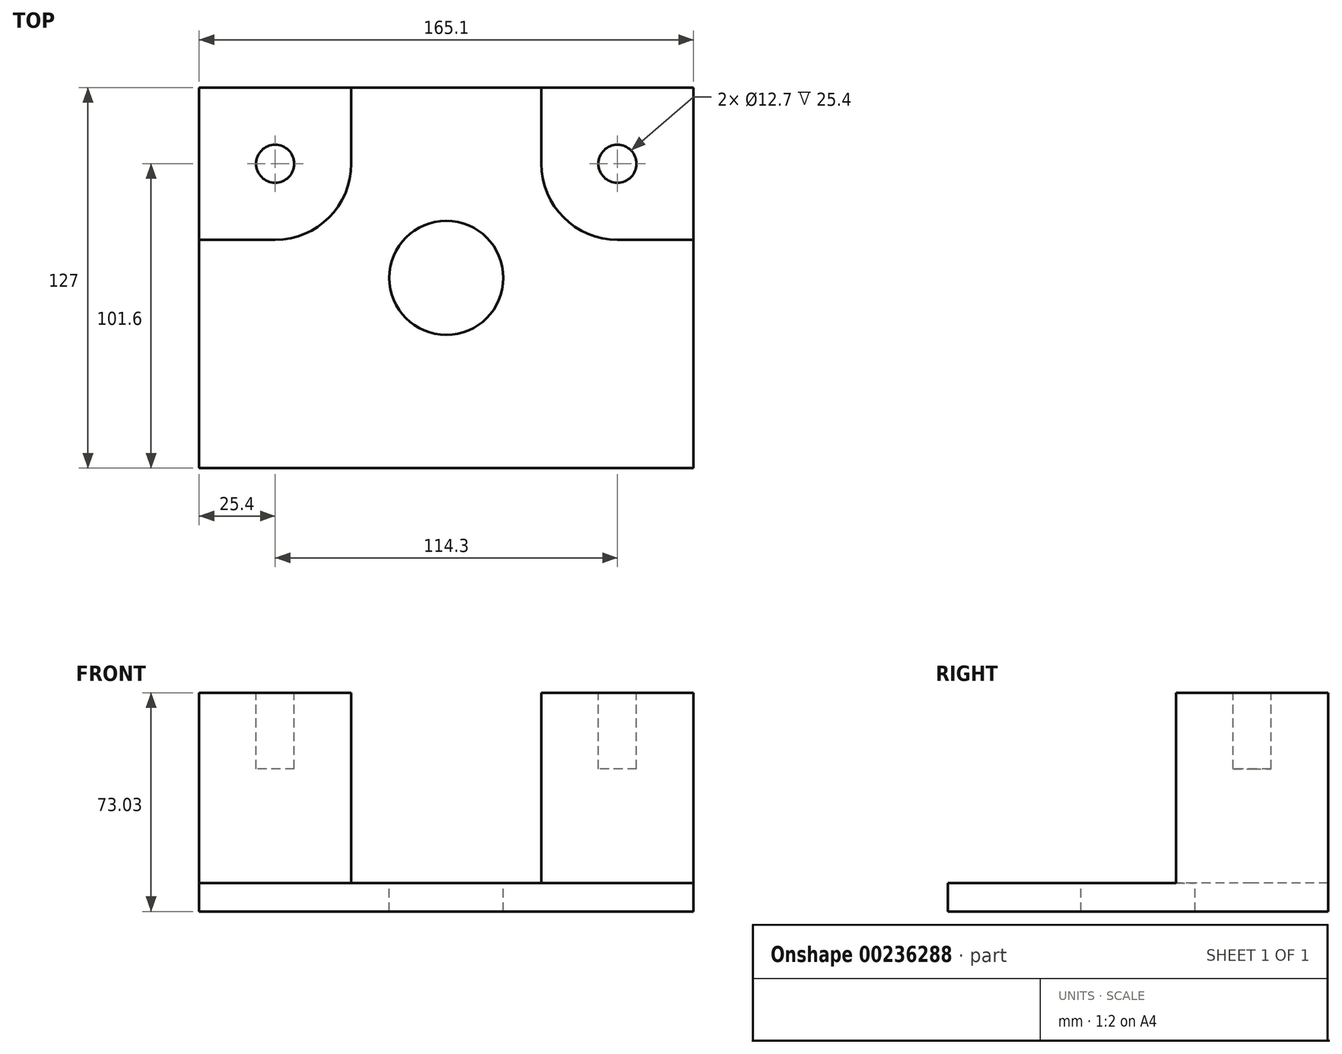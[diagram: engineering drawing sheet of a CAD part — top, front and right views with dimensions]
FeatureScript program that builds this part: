
annotation { "Feature Type Name" : "Feature", "Feature Type Description" : "" }
export const myFeature = defineFeature(function(context is Context, id is Id, definition is map)
    precondition{}
    {
        {
            var Q0;
            Q0=qCreatedBy(makeId("Top.planeOp"),FACE);
            var sketch = newSketch(context, id + "F0", { "sketchPlane" : qUnion([Q0])});
            skLineSegment(sketch, "E0.bottom", {"start": v(82.55, 63.5) * mm, "end": v(-82.55, 63.5) * mm});
            skLineSegment(sketch, "E0.top", {"start": v(82.55, -63.5) * mm, "end": v(-82.55, -63.5) * mm});
            skLineSegment(sketch, "E0.left", {"start": v(82.55, 63.5) * mm, "end": v(82.55, -63.5) * mm});
            skLineSegment(sketch, "E0.right", {"start": v(-82.55, 63.5) * mm, "end": v(-82.55, -63.5) * mm});
            skPoint(sketch, "E0.middle", {"position": v(0, 0) * mm});
            skSolve(sketch);
        }
        {
            var Q0;
            Q0 = qSketchRegion(id + "F0", true);
            extrude(context, id + "F1", {"entities" : qUnion([Q0]), "depth" : 9.52 * mm});
        }
        {
            var Q0;
            Q0=makeQuery(id+"F1.opExtrude","CAP_FACE",FACE,{"disambiguationData":[OSD([sQuery(id+"F0.wireOp",EDGE,"E0.bottom"),sQuery(id+"F0.wireOp",EDGE,"E0.top"),sQuery(id+"F0.wireOp",EDGE,"E0.left"),sQuery(id+"F0.wireOp",EDGE,"E0.right")])],"isStart":false});
            var sketch = newSketch(context, id + "F2", { "sketchPlane" : qUnion([Q0])});
            skLineSegment(sketch, "E1.bottom", {"start": v(-82.55, 63.5) * mm, "end": v(-31.75, 63.5) * mm});
            skLineSegment(sketch, "E1.top", {"start": v(-82.55, 12.7) * mm, "end": v(-57.15, 12.7) * mm});
            skLineSegment(sketch, "E1.left", {"start": v(-82.55, 63.5) * mm, "end": v(-82.55, 12.7) * mm});
            skLineSegment(sketch, "E1.right", {"start": v(-31.75, 63.5) * mm, "end": v(-31.75, 38.1) * mm});
            skLineSegment(sketch, "E2.bottom", {"start": v(82.55, 63.5) * mm, "end": v(31.75, 63.5) * mm});
            skLineSegment(sketch, "E2.top", {"start": v(82.55, 12.7) * mm, "end": v(57.15, 12.7) * mm});
            skLineSegment(sketch, "E2.left", {"start": v(82.55, 63.5) * mm, "end": v(82.55, 12.7) * mm});
            skLineSegment(sketch, "E2.right", {"start": v(31.75, 63.5) * mm, "end": v(31.75, 38.1) * mm});
            skPoint(sketch, "E3.visualSharp", {"position": v(-31.75, 12.7) * mm});
            skArc(sketch, "E3.filletArc", {"start": v(-57.15, 12.7) * mm, "mid": v(-39.19, 20.14) * mm, "end": v(-31.75, 38.1) * mm});
            skPoint(sketch, "E4.visualSharp", {"position": v(31.75, 12.7) * mm});
            skArc(sketch, "E4.filletArc", {"start": v(31.75, 38.1) * mm, "mid": v(39.19, 20.14) * mm, "end": v(57.15, 12.7) * mm});
            skSolve(sketch);
        }
        {
            var Q0;
            Q0=makeQuery(id+"F2.imprint","IMPRINT",FACE,{"disambiguationData":[TD([[makeQuery(id+"F2.imprint","IMPRINT",EDGE,{"derivedFrom":sQuery(id+"F2.wireOp",EDGE,"E1.bottom")}),1.0]])]});
            var Q1;
            Q1=makeQuery(id+"F2.imprint","IMPRINT",FACE,{"disambiguationData":[TD([[makeQuery(id+"F2.imprint","IMPRINT",EDGE,{"derivedFrom":sQuery(id+"F2.wireOp",EDGE,"E2.bottom")}),1.0]])]});
            extrude(context, id + "F3", {"entities" : qUnion([Q0, Q1]), "operationType" : NewBodyOperationType.ADD, "depth" : 63.5 * mm});
        }
        {
            var Q0;
            {var subQ0=sQuery(id+"F0.wireOp",EDGE,"E0.left");var subQ1=sQuery(id+"F0.wireOp",EDGE,"E0.bottom");var subQ2=sQuery(id+"F0.wireOp",EDGE,"E0.top");var subQ3=sQuery(id+"F0.wireOp",EDGE,"E0.right");Q0=makeQuery(id+"F3.boolean.opBoolean","SPLIT",FACE,{"disambiguationData":[TD([makeQuery(id+"F1.opExtrude","SWEPT_FACE",FACE,{"disambiguationData":[OSD([subQ1])]})])],"derivedFrom":makeQuery(id+"F1.opExtrude","CAP_FACE",FACE,{"disambiguationData":[OSD([subQ1,subQ2,subQ0,subQ3])],"isStart":false})});}
            var sketch = newSketch(context, id + "F4", { "sketchPlane" : qUnion([Q0])});
            skCircle(sketch, "E5", {"center": v(0, 0) * mm, "radius": 19.84 * mm});
            skSolve(sketch);
        }
        {
            var Q0;
            Q0=sQuery(id+"F4.wireOp",VERTEX,"E5.center");
            var Q1;
            Q1=makeQuery(id+"F1.opExtrude","SWEPT_BODY",BODY,{"disambiguationData":[OSD([sQuery(id+"F0.wireOp",EDGE,"E0.bottom"),sQuery(id+"F0.wireOp",EDGE,"E0.top"),sQuery(id+"F0.wireOp",EDGE,"E0.left"),sQuery(id+"F0.wireOp",EDGE,"E0.right")])]});
            hole(context, id + "F5", {"style" : HoleStyle.SIMPLE, "endStyle" : HoleEndStyle.THROUGH, "holeDiameter" : 38.1 * mm, "locations" : qUnion([Q0]), "scope" : qUnion([Q1]), "isTappedThrough" : true});
        }
        {
            var Q0;
            Q0=makeQuery(id+"F3.opExtrude","CAP_FACE",FACE,{"disambiguationData":[OSD([sQuery(id+"F2.wireOp",EDGE,"E1.bottom"),sQuery(id+"F2.wireOp",EDGE,"E1.top"),sQuery(id+"F2.wireOp",EDGE,"E1.left"),sQuery(id+"F2.wireOp",EDGE,"E1.right"),sQuery(id+"F2.wireOp",EDGE,"E3.filletArc")])],"isStart":false});
            var sketch = newSketch(context, id + "F6", { "sketchPlane" : qUnion([Q0])});
            skCircle(sketch, "E6", {"center": v(-57.15, 38.1) * mm, "radius": 6.35 * mm});
            skCircle(sketch, "E7", {"center": v(57.15, 38.1) * mm, "radius": 6.35 * mm});
            skSolve(sketch);
        }
        {
            var Q0;
            Q0=makeQuery(id+"F6.imprint","IMPRINT",FACE,{"disambiguationData":[TD([[makeQuery(id+"F6.imprint","IMPRINT",EDGE,{"derivedFrom":sQuery(id+"F6.wireOp",EDGE,"E6")}),1.0]])]});
            var Q1;
            Q1=makeQuery(id+"F6.imprint","IMPRINT",FACE,{"disambiguationData":[TD([[makeQuery(id+"F6.imprint","IMPRINT",EDGE,{"derivedFrom":sQuery(id+"F6.wireOp",EDGE,"E7")}),1.0]])]});
            var Q2;
            Q2=sQuery(id+"F6.wireOp",EDGE,"E6");
            extrude(context, id + "F7", {"entities" : qUnion([Q0, Q1]), "operationType" : NewBodyOperationType.REMOVE, "surfaceEntities" : qUnion([Q2]), "oppositeDirection" : true, "depth" : 25.4 * mm});
        }
    });
